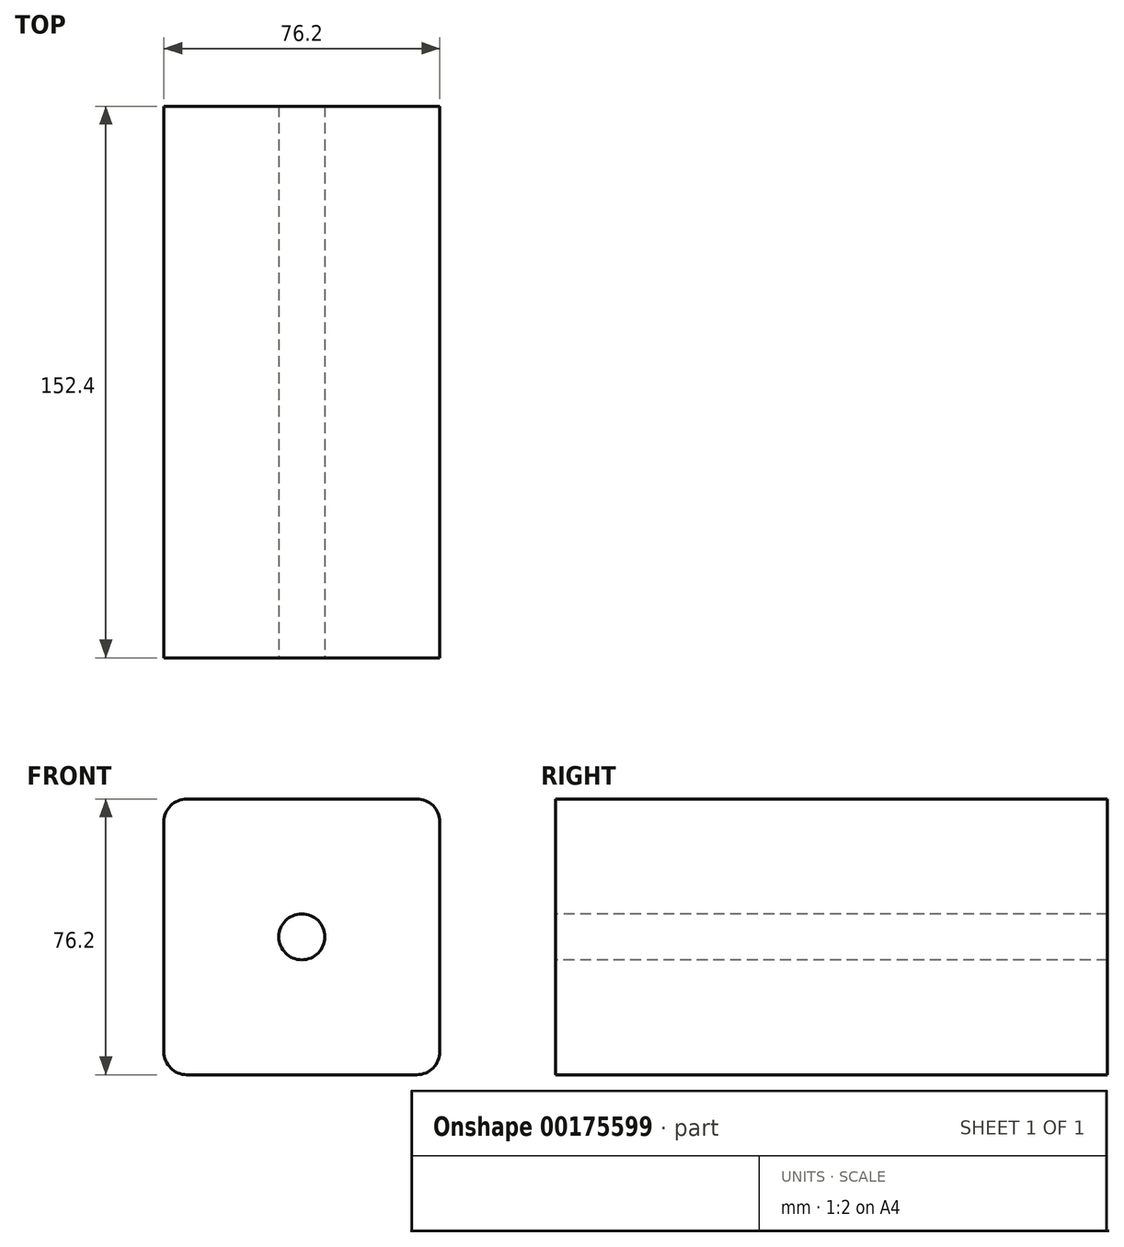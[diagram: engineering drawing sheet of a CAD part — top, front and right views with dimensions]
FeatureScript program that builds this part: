
annotation { "Feature Type Name" : "Feature", "Feature Type Description" : "" }
export const myFeature = defineFeature(function(context is Context, id is Id, definition is map)
    precondition{}
    {
        {
            var Q0;
            Q0=qCreatedBy(makeId("Front.planeOp"),FACE);
            var sketch = newSketch(context, id + "F0", { "sketchPlane" : qUnion([Q0])});
            skLineSegment(sketch, "E0.bottom", {"start": v(-38.1, 38.1) * mm, "end": v(38.1, 38.1) * mm});
            skLineSegment(sketch, "E0.top", {"start": v(-38.1, -38.1) * mm, "end": v(38.1, -38.1) * mm});
            skLineSegment(sketch, "E0.left", {"start": v(-38.1, 38.1) * mm, "end": v(-38.1, -38.1) * mm});
            skLineSegment(sketch, "E0.right", {"start": v(38.1, 38.1) * mm, "end": v(38.1, -38.1) * mm});
            skLineSegment(sketch, "E1", {"start": v(0, 38.1) * mm, "end": v(0, -38.1) * mm, "construction": true});
            skSolve(sketch);
        }
        {
            var Q0;
            Q0 = qSketchRegion(id + "F0", true);
            extrude(context, id + "F1", {"entities" : qUnion([Q0]), "endBound" : BoundingType.SYMMETRIC, "depth" : 152.4 * mm});
        }
        {
            var Q0;
            Q0=makeQuery(id+"F1.opExtrude","CAP_FACE",FACE,{"disambiguationData":[OSD([sQuery(id+"F0.wireOp",EDGE,"E0.bottom"),sQuery(id+"F0.wireOp",EDGE,"E0.top"),sQuery(id+"F0.wireOp",EDGE,"E0.left"),sQuery(id+"F0.wireOp",EDGE,"E0.right")])],"isStart":false});
            var sketch = newSketch(context, id + "F2", { "sketchPlane" : qUnion([Q0])});
            skPoint(sketch, "E2", {"position": v(0, 0) * mm});
            skSolve(sketch);
        }
        {
            var Q0;
            Q0=sQuery(id+"F2.wireOp",VERTEX,"E2");
            var Q1;
            Q1=makeQuery(id+"F1.opExtrude","SWEPT_BODY",BODY,{"disambiguationData":[OSD([sQuery(id+"F0.wireOp",EDGE,"E0.bottom"),sQuery(id+"F0.wireOp",EDGE,"E0.top"),sQuery(id+"F0.wireOp",EDGE,"E0.left"),sQuery(id+"F0.wireOp",EDGE,"E0.right")])]});
            hole(context, id + "F3", {"style" : HoleStyle.SIMPLE, "endStyle" : HoleEndStyle.THROUGH, "holeDiameter" : 12.7 * mm, "locations" : qUnion([Q0]), "scope" : qUnion([Q1]), "isTappedThrough" : true});
        }
        {
            var Q0;
            Q0=makeQuery(id+"F1.opExtrude","SWEPT_EDGE",EDGE,{"disambiguationData":[OSD([sQuery(id+"F0.wireOp",EDGE,"E0.bottom"),sQuery(id+"F0.wireOp",EDGE,"E0.left")])]});
            var Q1;
            Q1=makeQuery(id+"F1.opExtrude","SWEPT_EDGE",EDGE,{"disambiguationData":[OSD([sQuery(id+"F0.wireOp",EDGE,"E0.bottom"),sQuery(id+"F0.wireOp",EDGE,"E0.right")])]});
            var Q2;
            Q2=makeQuery(id+"F1.opExtrude","SWEPT_EDGE",EDGE,{"disambiguationData":[OSD([sQuery(id+"F0.wireOp",EDGE,"E0.top"),sQuery(id+"F0.wireOp",EDGE,"E0.right")])]});
            var Q3;
            Q3=makeQuery(id+"F1.opExtrude","SWEPT_EDGE",EDGE,{"disambiguationData":[OSD([sQuery(id+"F0.wireOp",EDGE,"E0.top"),sQuery(id+"F0.wireOp",EDGE,"E0.left")])]});
            fillet(context, id + "F4", {"entities" : qUnion([Q0, Q1, Q2, Q3]), "radius" : 6.35 * mm, "tangentPropagation" : true, "allowEdgeOverflow" : false});
        }
    });
